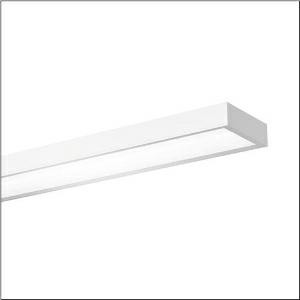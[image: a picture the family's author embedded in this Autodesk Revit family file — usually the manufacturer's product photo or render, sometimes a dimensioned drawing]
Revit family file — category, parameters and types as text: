
# Revit family: sport_31_51hs12dc3dca
name_source: partatom
category: Lighting Fixtures
units: mm (PartAtom-declared; Revit-internal decimal feet)

## family parameters
Cut with Voids When Loaded = No
Host = Face
Light Source = No
Part Type = Normal
Room Calculation Point = No
Round Connector Dimension = Use Diameter
Shared = No

## types (1)
- --- (1 x LED, 7500 lm, 55.4 W, 3000K)
    Apparent Load = 55 VA
    CIE Flux Codes = 65 89 97 100 100
    Color Rendering = 80
    Color Temperature = 3000K
    Default Elevation = 1800 mm
    Description = Sport 31, LED high bay luminaire, primary light control with reflector, of sheet steel, primary anti-glare with prismatic structure, of PC, primary optical cover: cover panel, of PC, light emission: direct distribution, primary light characteristic: symmetric, installation type: suspended mounting, recessed, surface-mounted, LED, rated luminous flux: 7.500lm, luminous efficacy: 130lm/W, light colour: 830, colour temperature: 3000K, control gear: DALI 2, with terminal, 5-pole, max. 2.5mm², mains connection: 220..240V, AC/DC, 50/60Hz, rated input power: 58W, housing, of sheet steel, traffic white (RAL 9016), length: 1.540mm, width: 315mm, height: 95mm, protection rating (complete): IP20, protection rating (lamp compartment, on room side): IP50, insulation class (complete): insulation class I (protective earthing), certification: CE, ENEC, UKCA, ball protection: ball impact resistant with ceiling mounting or chain suspension, impact resistance: IK08, permissible operating ambient temperature: -20..+35°C, standard: DIN 18032-3, EN 60598-2-22, packaging unit: 1 piece
    Height = 100 mm  [stored 0.328084 ft]
    Lamp = 1 x LED
    Lamp Light Flux = 7500 lm
    Lamp Power = 55.4 W
    Lamp count = 1
    Length = 1500 mm
    Luminous efficacy = 135 lm/W
    Manufacturer = Siteco
    ModVariant = No
    Model = 51HS12DC3DCA
    Mounting Place = Ceiling
    Mounting Type = Pendant
    Number of Poles = 1
    OnlyDefault = Yes
    Power Factor = 1
    Product Name = Sport 31
    Product group = LED high bay luminaire
    ProductGroupID = 903
    Protection Class = Protection class I
    Protection Degree = IP 20
    RLX_Detail_Level = 1
    RLX_Emergency_Light_Flux = 0 lm
    RLX_Emergency_Type = 0
    RLX_Emergency_Type_DB = No
    RlxData = <blob elided: 22745 chars, md5=ed44ecf9>
    Socket = socket
    Standby Power = 0 W
    System Light Flux = 7500 lm
    System Power = 55 W
    Type Comments = factory setting: luminous flux: 100 % | dim-lin: 254 | 234 mA
    Type Image = l_1006823.jpg
    URL = http://relux.com
    VarID = @adj_197258
    Voltage = 0 V
    Weight = 0.00 kg
    Width = 315 mm

note: [stored X ft] marks values corroborated as IEEE doubles in the binary element streams (Revit-internal decimal feet)

## geometry (parser evidence)
native form markers: Blend x4, Sweep x9
no freeform markers — native parametric forms only
